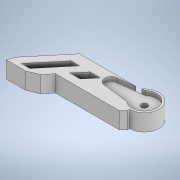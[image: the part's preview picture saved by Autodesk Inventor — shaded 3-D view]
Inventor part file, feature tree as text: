
AUTODESK INVENTOR PART (.ipt)
format: ipt  version: 2021 (Build 250183000, 183)  size: 224,768 bytes
history: native  units: mm
features: extrude x8, sketch x8, other x1, chamfer x1
ambient origin geometry x8: Origin, YZ Plane, XZ Plane, XY Plane, X Axis, Y Axis, Z Axis, Center Point
bodies: Body1 (feature_tree)
feature tree (18):
  other  "Sólido1"
  extrude  "Extrusión1"  Depth=6.0mm
  extrude  "Extrusión2"  Depth=5.0mm
  extrude  "Extrusión6"  Depth=5.0mm
  chamfer  "Chaflán1"  Distance=5.0mm
  extrude  "Extrusión9"  Depth=10.0mm TaperAngle=0.0deg
  extrude  "Extrusión10"  Depth=2.0mm TaperAngle=45.0deg
  extrude  "Extrusión13"  Depth=6.0mm
  extrude  "Extrusión14"  Depth=4.0mm TaperAngle=0.0deg
  extrude  "Extrusión16"  Depth=10.0mm
  sketch  "Boceto1"  dims[d10=8.0mm d11=0.0mm d12=6.0mm]
  sketch  "Boceto2"  dims[d13=4.0mm d14=0.0mm d28=5.0mm]
  sketch  "Boceto6"  dims[d29=5.0mm d30=5.0mm]
  sketch  "Boceto9"  dims[d31=5.0mm]
  sketch  "Boceto10"  dims[d32=5.0mm]
  sketch  "Boceto14"  dims[d33=5.0mm]
  sketch  "Boceto15"  dims[d34=5.0mm]
  sketch  "Boceto17"  dims[d35=5.0mm d36=5.0mm d37=10.0mm d38=0.0mm d44=2.0mm d45=2.0mm d46=45.0deg d47=6.0mm d48=4.0mm d49=0.0mm d50=12.0mm d51=19.0mm d52=4.5mm d53=9.0mm d54=3.0mm d55=2.0mm d56=0.0mm d68=8.0mm d69=0.0mm d70=8.0mm d71=0.0mm d82=10.0mm d83=0.0mm d25=0.5mm d26=0.872665mm d27=0.5mm d39=0.5mm d40=0.872665mm]
